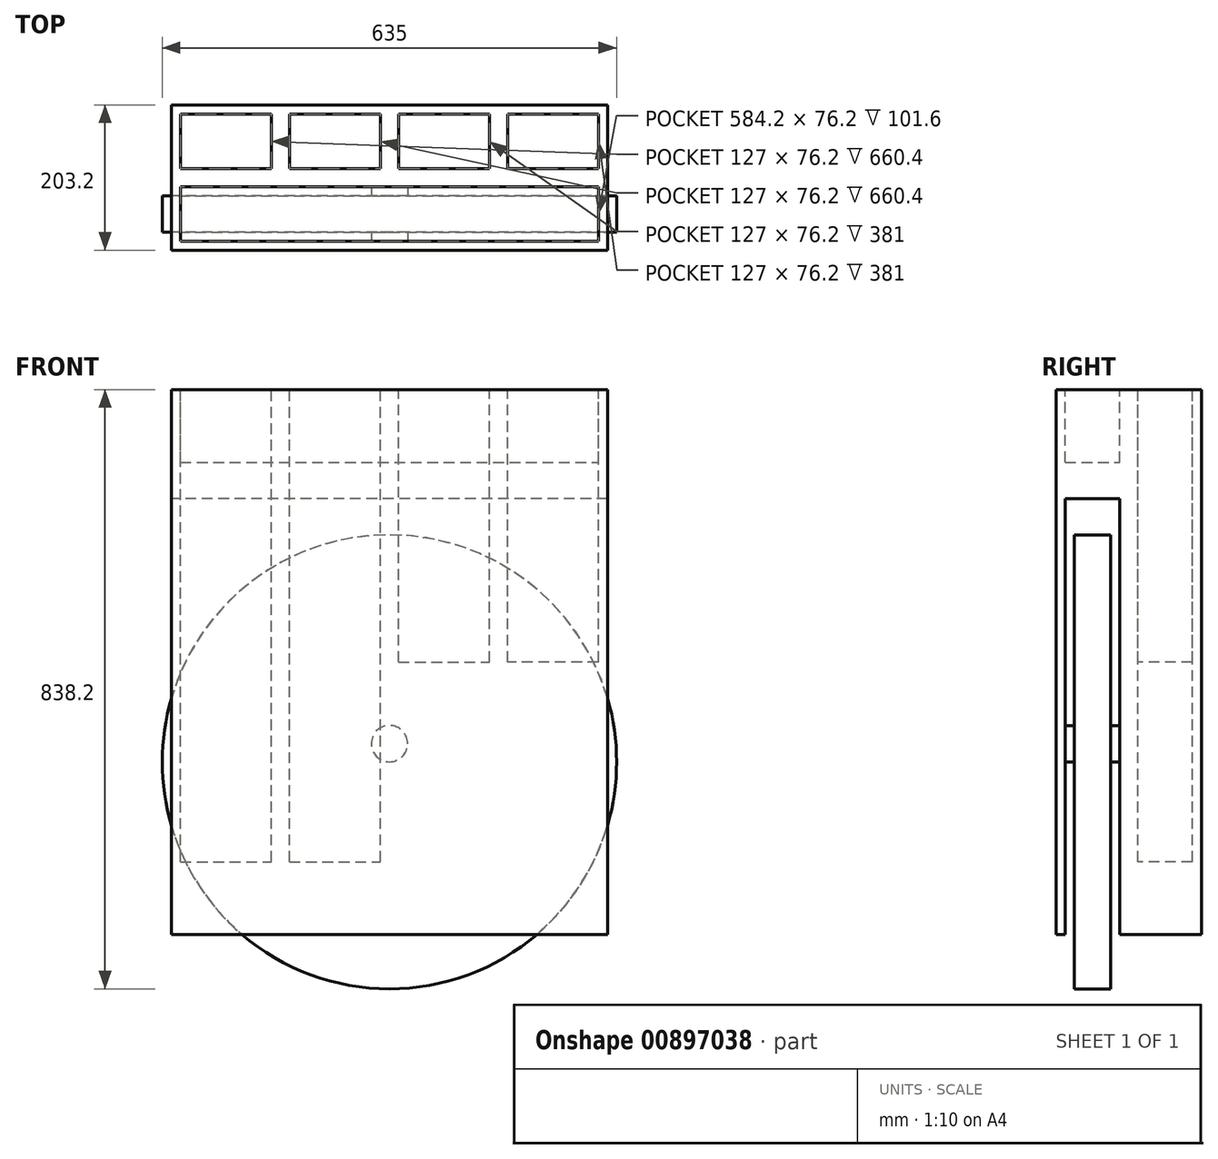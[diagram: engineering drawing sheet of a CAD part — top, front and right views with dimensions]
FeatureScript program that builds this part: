
annotation { "Feature Type Name" : "Feature", "Feature Type Description" : "" }
export const myFeature = defineFeature(function(context is Context, id is Id, definition is map)
    precondition{}
    {
        {
            var Q0;
            Q0=qCreatedBy(makeId("Front.planeOp"),FACE);
            var sketch = newSketch(context, id + "F0", { "sketchPlane" : qUnion([Q0])});
            skLineSegment(sketch, "E0.bottom", {"start": v(316.92, 381) * mm, "end": v(-292.68, 381) * mm});
            skLineSegment(sketch, "E0.top", {"start": v(316.92, -381) * mm, "end": v(-292.68, -381) * mm});
            skLineSegment(sketch, "E0.left", {"start": v(316.92, 381) * mm, "end": v(316.92, -381) * mm});
            skLineSegment(sketch, "E0.right", {"start": v(-292.68, 381) * mm, "end": v(-292.68, -381) * mm});
            skPoint(sketch, "E0.middle", {"position": v(12.12, 0) * mm});
            skSolve(sketch);
        }
        {
            var Q0;
            Q0 = qSketchRegion(id + "F0", true);
            extrude(context, id + "F1", {"entities" : qUnion([Q0]), "depth" : 203.2 * mm, "offsetDistance" : 25.4 * mm});
        }
        {
            var Q0;
            Q0=makeQuery(id+"F1.opExtrude","SWEPT_FACE",FACE,{"disambiguationData":[OSD([sQuery(id+"F0.wireOp",EDGE,"E0.right")])]});
            var sketch = newSketch(context, id + "F2", { "sketchPlane" : qUnion([Q0])});
            skLineSegment(sketch, "E1.bottom", {"start": v(190.5, -381) * mm, "end": v(114.3, -381) * mm});
            skLineSegment(sketch, "E1.top", {"start": v(190.5, 228.6) * mm, "end": v(114.3, 228.6) * mm});
            skLineSegment(sketch, "E1.left", {"start": v(190.5, -381) * mm, "end": v(190.5, 228.6) * mm});
            skLineSegment(sketch, "E1.right", {"start": v(114.3, -381) * mm, "end": v(114.3, 228.6) * mm});
            skSolve(sketch);
        }
        {
            var Q0;
            Q0=makeQuery(id+"F2.imprint","IMPRINT",FACE,{"disambiguationData":[TD([[makeQuery(id+"F2.imprint","IMPRINT",EDGE,{"derivedFrom":sQuery(id+"F2.wireOp",EDGE,"E1.bottom")}),-1.0]])]});
            extrude(context, id + "F3", {"entities" : qUnion([Q0]), "operationType" : NewBodyOperationType.REMOVE, "oppositeDirection" : true, "depth" : 609.6 * mm, "offsetDistance" : 25.4 * mm});
        }
        {
            var Q0;
            Q0=makeQuery(id+"F1.opExtrude","SWEPT_FACE",FACE,{"disambiguationData":[OSD([sQuery(id+"F0.wireOp",EDGE,"E0.bottom")])]});
            var sketch = newSketch(context, id + "F4", { "sketchPlane" : qUnion([Q0])});
            skLineSegment(sketch, "E2.bottom", {"start": v(-279.98, -190.5) * mm, "end": v(304.22, -190.5) * mm});
            skLineSegment(sketch, "E2.top", {"start": v(-279.98, -114.3) * mm, "end": v(304.22, -114.3) * mm});
            skLineSegment(sketch, "E2.left", {"start": v(-279.98, -190.5) * mm, "end": v(-279.98, -114.3) * mm});
            skLineSegment(sketch, "E2.right", {"start": v(304.22, -190.5) * mm, "end": v(304.22, -114.3) * mm});
            skSolve(sketch);
        }
        {
            var Q0;
            Q0=makeQuery(id+"F4.imprint","IMPRINT",FACE,{"disambiguationData":[TD([[makeQuery(id+"F4.imprint","IMPRINT",EDGE,{"derivedFrom":sQuery(id+"F4.wireOp",EDGE,"E2.bottom")}),1.0]])]});
            extrude(context, id + "F5", {"entities" : qUnion([Q0]), "operationType" : NewBodyOperationType.REMOVE, "oppositeDirection" : true, "depth" : 101.6 * mm, "offsetDistance" : 25.4 * mm});
        }
        {
            var Q0;
            Q0=makeQuery(id+"F1.opExtrude","SWEPT_FACE",FACE,{"disambiguationData":[OSD([sQuery(id+"F0.wireOp",EDGE,"E0.bottom")])]});
            var sketch = newSketch(context, id + "F6", { "sketchPlane" : qUnion([Q0])});
            skSolve(sketch);
        }
        {
            var Q0;
            Q0=makeQuery(id+"F1.opExtrude","SWEPT_FACE",FACE,{"disambiguationData":[OSD([sQuery(id+"F0.wireOp",EDGE,"E0.bottom")])]});
            var sketch = newSketch(context, id + "F7", { "sketchPlane" : qUnion([Q0])});
            skLineSegment(sketch, "E3.bottom", {"start": v(-279.98, -12.7) * mm, "end": v(-152.98, -12.7) * mm});
            skLineSegment(sketch, "E3.top", {"start": v(-279.98, -88.9) * mm, "end": v(-152.98, -88.9) * mm});
            skLineSegment(sketch, "E3.left", {"start": v(-279.98, -12.7) * mm, "end": v(-279.98, -88.9) * mm});
            skLineSegment(sketch, "E3.right", {"start": v(-152.98, -12.7) * mm, "end": v(-152.98, -88.9) * mm});
            skSolve(sketch);
        }
        {
            var Q0;
            Q0=makeQuery(id+"F7.imprint","IMPRINT",FACE,{"disambiguationData":[TD([[makeQuery(id+"F7.imprint","IMPRINT",EDGE,{"derivedFrom":sQuery(id+"F7.wireOp",EDGE,"E3.bottom")}),-1.0]])]});
            extrude(context, id + "F8", {"entities" : qUnion([Q0]), "operationType" : NewBodyOperationType.REMOVE, "oppositeDirection" : true, "depth" : 660.4 * mm, "offsetDistance" : 25.4 * mm});
        }
        {
            var Q0;
            {var subQ0=sQuery(id+"F0.wireOp",EDGE,"E0.bottom");Q0=makeQuery(id+"F6.imprint","IMPRINT",FACE,{"disambiguationData":[TD([[makeQuery(id+"F6.imprint","IMPRINT",EDGE,{"derivedFrom":makeQuery(id+"F1.opExtrude","CAP_EDGE",EDGE,{"disambiguationData":[OSD([subQ0])],"isStart":true})}),1.0]])]});}
            var sketch = newSketch(context, id + "F9", { "sketchPlane" : qUnion([Q0])});
            skLineSegment(sketch, "E4.bottom", {"start": v(-127.58, -12.7) * mm, "end": v(-0.58, -12.7) * mm});
            skLineSegment(sketch, "E4.top", {"start": v(-127.58, -88.9) * mm, "end": v(-0.58, -88.9) * mm});
            skLineSegment(sketch, "E4.left", {"start": v(-127.58, -12.7) * mm, "end": v(-127.58, -88.9) * mm});
            skLineSegment(sketch, "E4.right", {"start": v(-0.58, -12.7) * mm, "end": v(-0.58, -88.9) * mm});
            skSolve(sketch);
        }
        {
            var Q0;
            Q0=makeQuery(id+"F9.imprint","IMPRINT",FACE,{"disambiguationData":[TD([[makeQuery(id+"F9.imprint","IMPRINT",EDGE,{"derivedFrom":sQuery(id+"F9.wireOp",EDGE,"E4.bottom")}),-1.0]])]});
            extrude(context, id + "F10", {"entities" : qUnion([Q0]), "operationType" : NewBodyOperationType.REMOVE, "oppositeDirection" : true, "depth" : 660.4 * mm, "offsetDistance" : 25.4 * mm});
        }
        {
            var Q0;
            {var subQ0=sQuery(id+"F0.wireOp",EDGE,"E0.bottom");Q0=makeQuery(id+"F6.imprint","IMPRINT",FACE,{"disambiguationData":[TD([[makeQuery(id+"F6.imprint","IMPRINT",EDGE,{"derivedFrom":makeQuery(id+"F1.opExtrude","CAP_EDGE",EDGE,{"disambiguationData":[OSD([subQ0])],"isStart":true})}),1.0]])]});}
            var sketch = newSketch(context, id + "F11", { "sketchPlane" : qUnion([Q0])});
            skLineSegment(sketch, "E5.bottom", {"start": v(24.82, -12.7) * mm, "end": v(151.82, -12.7) * mm});
            skLineSegment(sketch, "E5.top", {"start": v(24.82, -88.9) * mm, "end": v(151.82, -88.9) * mm});
            skLineSegment(sketch, "E5.left", {"start": v(24.82, -12.7) * mm, "end": v(24.82, -88.9) * mm});
            skLineSegment(sketch, "E5.right", {"start": v(151.82, -12.7) * mm, "end": v(151.82, -88.9) * mm});
            skSolve(sketch);
        }
        {
            var Q0;
            {var subQ0=sQuery(id+"F0.wireOp",EDGE,"E0.bottom");Q0=makeQuery(id+"F6.imprint","IMPRINT",FACE,{"disambiguationData":[TD([[makeQuery(id+"F6.imprint","IMPRINT",EDGE,{"derivedFrom":makeQuery(id+"F1.opExtrude","CAP_EDGE",EDGE,{"disambiguationData":[OSD([subQ0])],"isStart":true})}),1.0]])]});}
            var sketch = newSketch(context, id + "F12", { "sketchPlane" : qUnion([Q0])});
            skLineSegment(sketch, "E6.bottom", {"start": v(304.22, -12.7) * mm, "end": v(177.22, -12.7) * mm});
            skLineSegment(sketch, "E6.top", {"start": v(304.22, -88.9) * mm, "end": v(177.22, -88.9) * mm});
            skLineSegment(sketch, "E6.left", {"start": v(304.22, -12.7) * mm, "end": v(304.22, -88.9) * mm});
            skLineSegment(sketch, "E6.right", {"start": v(177.22, -12.7) * mm, "end": v(177.22, -88.9) * mm});
            skSolve(sketch);
        }
        {
            var Q0;
            Q0=makeQuery(id+"F11.imprint","IMPRINT",FACE,{"disambiguationData":[TD([[makeQuery(id+"F11.imprint","IMPRINT",EDGE,{"derivedFrom":sQuery(id+"F11.wireOp",EDGE,"E5.bottom")}),-1.0]])]});
            extrude(context, id + "F13", {"entities" : qUnion([Q0]), "operationType" : NewBodyOperationType.REMOVE, "oppositeDirection" : true, "depth" : 381 * mm, "offsetDistance" : 25.4 * mm});
        }
        {
            var Q0;
            Q0 = qSketchRegion(id + "F11", true);
            extrude(context, id + "F14", {"entities" : qUnion([Q0]), "operationType" : NewBodyOperationType.REMOVE, "oppositeDirection" : true, "depth" : 381 * mm, "offsetDistance" : 25.4 * mm});
        }
        {
            var Q0;
            Q0=makeQuery(id+"F12.imprint","IMPRINT",FACE,{"disambiguationData":[TD([[makeQuery(id+"F12.imprint","IMPRINT",EDGE,{"derivedFrom":sQuery(id+"F12.wireOp",EDGE,"E6.bottom")}),1.0]])]});
            extrude(context, id + "F15", {"entities" : qUnion([Q0]), "operationType" : NewBodyOperationType.REMOVE, "oppositeDirection" : true, "depth" : 381 * mm, "offsetDistance" : 25.4 * mm});
        }
        {
            var Q0;
            Q0=makeQuery(id+"F1.opExtrude","CAP_FACE",FACE,{"disambiguationData":[OSD([sQuery(id+"F0.wireOp",EDGE,"E0.bottom"),sQuery(id+"F0.wireOp",EDGE,"E0.top"),sQuery(id+"F0.wireOp",EDGE,"E0.left"),sQuery(id+"F0.wireOp",EDGE,"E0.right")])],"isStart":false});
            var sketch = newSketch(context, id + "F16", { "sketchPlane" : qUnion([Q0])});
            skCircle(sketch, "E7", {"center": v(12.12, -114.3) * mm, "radius": 25.4 * mm});
            skPoint(sketch, "E7.centerSnap0", {"position": v(12.12, 381) * mm});
            skSolve(sketch);
        }
        {
            var Q0;
            Q0=makeQuery(id+"F16.imprint","IMPRINT",FACE,{"disambiguationData":[TD([[makeQuery(id+"F16.imprint","IMPRINT",EDGE,{"derivedFrom":sQuery(id+"F16.wireOp",EDGE,"E7")}),1.0]])]});
            extrude(context, id + "F17", {"entities" : qUnion([Q0]), "operationType" : NewBodyOperationType.ADD, "oppositeDirection" : true, "depth" : 88.9 * mm, "offsetDistance" : 25.4 * mm});
        }
        {
            var Q0;
            Q0=makeQuery(id+"F3.boolean.opBoolean","COPY",FACE,{"derivedFrom":makeQuery(id+"F3.opExtrude","SWEPT_FACE",FACE,{"disambiguationData":[OSD([sQuery(id+"F2.wireOp",EDGE,"E1.right")])]})});
            cPlane(context, id + "F18", {"entities" : qUnion([Q0]), "cplaneType" : CPlaneType.OFFSET, "offset" : 12.7 * mm, "width" : 152.4 * mm, "height" : 152.4 * mm});
        }
        {
            var Q0;
            Q0=qCreatedBy(id+"F18.planeOp",FACE);
            var sketch = newSketch(context, id + "F19", { "sketchPlane" : qUnion([Q0])});
            skCircle(sketch, "E8", {"center": v(12.12, -139.7) * mm, "radius": 317.5 * mm});
            skSolve(sketch);
        }
        {
            var Q0;
            Q0=makeQuery(id+"F19.imprint","IMPRINT",FACE,{"disambiguationData":[TD([[makeQuery(id+"F19.imprint","IMPRINT",EDGE,{"derivedFrom":sQuery(id+"F19.wireOp",EDGE,"E8")}),1.0]])]});
            extrude(context, id + "F20", {"entities" : qUnion([Q0]), "operationType" : NewBodyOperationType.ADD, "depth" : 50.8 * mm, "offsetDistance" : 25.4 * mm});
        }
    });
